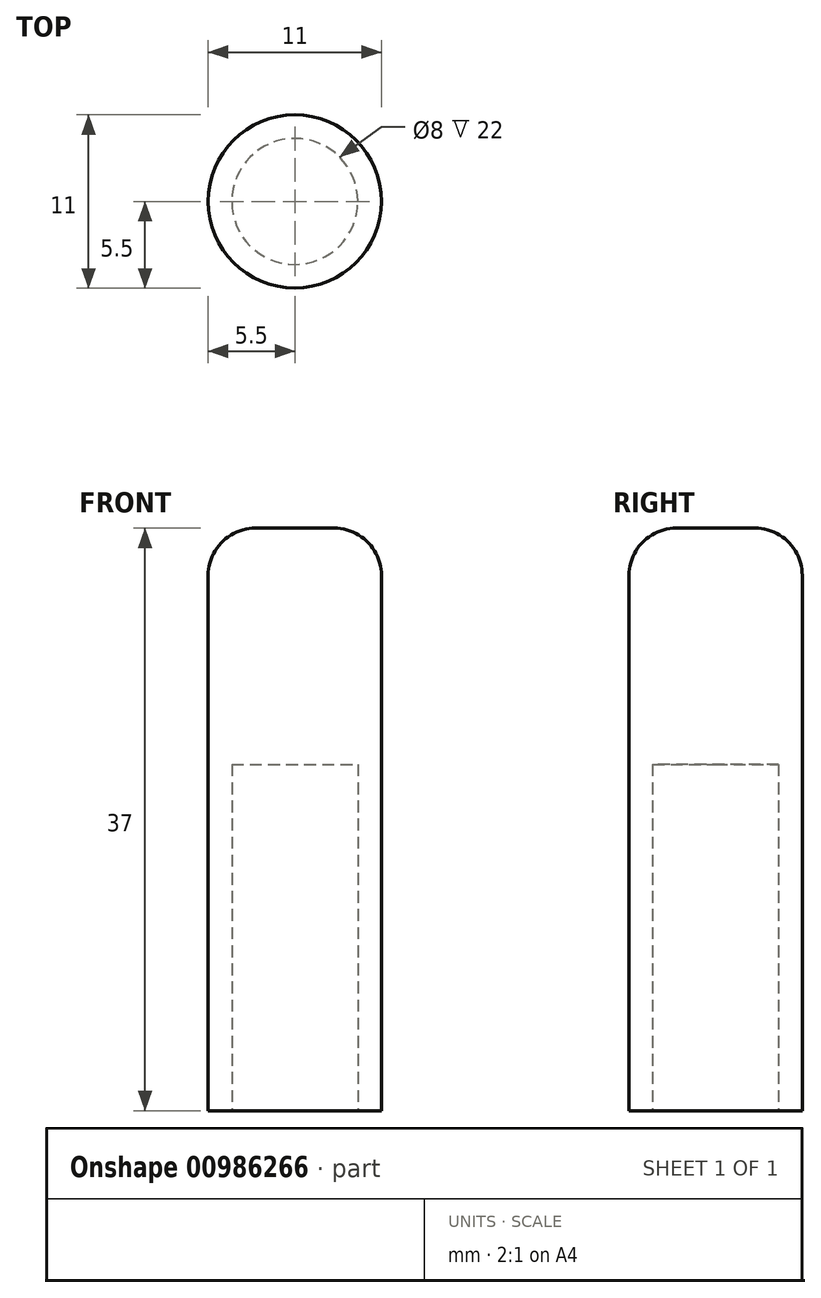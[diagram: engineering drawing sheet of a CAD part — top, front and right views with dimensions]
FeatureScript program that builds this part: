
annotation { "Feature Type Name" : "Feature", "Feature Type Description" : "" }
export const myFeature = defineFeature(function(context is Context, id is Id, definition is map)
    precondition{}
    {
        {
            var Q0;
            Q0=qCreatedBy(makeId("Top.planeOp"),FACE);
            var sketch = newSketch(context, id + "F0", { "sketchPlane" : qUnion([Q0])});
            skCircle(sketch, "E0", {"center": v(0, 0) * mm, "radius": 5.5 * mm});
            skSolve(sketch);
        }
        {
            var Q0;
            Q0=makeQuery(id+"F0.imprint","IMPRINT",FACE,{"disambiguationData":[TD([[makeQuery(id+"F0.imprint","IMPRINT",EDGE,{"derivedFrom":sQuery(id+"F0.wireOp",EDGE,"E0")}),1.0]])]});
            extrude(context, id + "F1", {"entities" : qUnion([Q0]), "depth" : 25 * mm, "offsetDistance" : 25 * mm});
        }
        {
            var Q0;
            Q0=makeQuery(id+"F1.opExtrude","CAP_FACE",FACE,{"disambiguationData":[OSD([sQuery(id+"F0.wireOp",EDGE,"E0")])],"isStart":true});
            var sketch = newSketch(context, id + "F2", { "sketchPlane" : qUnion([Q0])});
            skCircle(sketch, "E1", {"center": v(0, 0) * mm, "radius": 4 * mm});
            skSolve(sketch);
        }
        {
            var Q0;
            Q0=makeQuery(id+"F2.imprint","IMPRINT",FACE,{"disambiguationData":[TD([[makeQuery(id+"F2.imprint","IMPRINT",EDGE,{"derivedFrom":sQuery(id+"F2.wireOp",EDGE,"E1")}),1.0]])]});
            extrude(context, id + "F3", {"entities" : qUnion([Q0]), "operationType" : NewBodyOperationType.REMOVE, "oppositeDirection" : true, "depth" : 10 * mm, "offsetDistance" : 25 * mm});
        }
        {
            var Q0;
            Q0=makeQuery(id+"F1.opExtrude","CAP_EDGE",EDGE,{"disambiguationData":[OSD([sQuery(id+"F0.wireOp",EDGE,"E0")])],"isStart":false});
            fillet(context, id + "F4", {"entities" : qUnion([Q0]), "radius" : 3 * mm, "tangentPropagation" : true, "allowEdgeOverflow" : false});
        }
        {
            var Q0;
            Q0=makeQuery(id+"F1.opExtrude","CAP_FACE",FACE,{"disambiguationData":[OSD([sQuery(id+"F0.wireOp",EDGE,"E0")])],"isStart":true});
            extrude(context, id + "F5", {"entities" : qUnion([Q0]), "operationType" : NewBodyOperationType.ADD, "depth" : 12 * mm, "offsetDistance" : 25 * mm});
        }
    });
